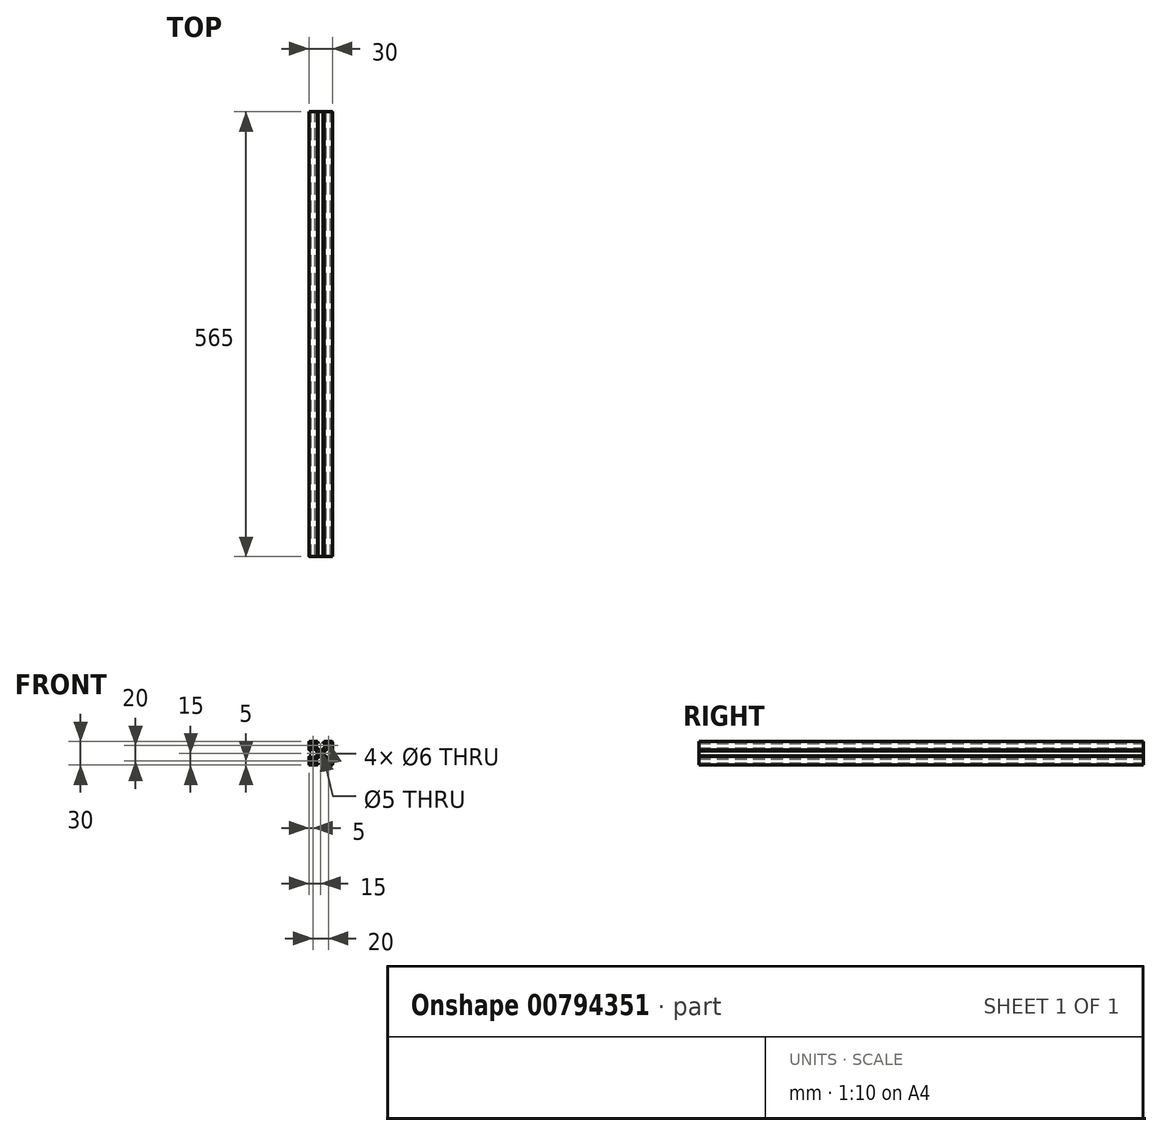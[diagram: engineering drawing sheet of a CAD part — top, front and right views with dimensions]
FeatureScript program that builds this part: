
annotation { "Feature Type Name" : "Feature", "Feature Type Description" : "" }
export const myFeature = defineFeature(function(context is Context, id is Id, definition is map)
    precondition{}
    {
        {
            var Q0;
            Q0=qCreatedBy(makeId("Front.planeOp"),FACE);
            var sketch = newSketch(context, id + "F0", { "sketchPlane" : qUnion([Q0])});
            skCircle(sketch, "E0", {"center": v(0, 0) * mm, "radius": 2.5 * mm});
            skCircle(sketch, "E1", {"center": v(-10, 10) * mm, "radius": 3 * mm});
            skCircle(sketch, "E2", {"center": v(10, 10) * mm, "radius": 3 * mm});
            skCircle(sketch, "E3", {"center": v(10, -10) * mm, "radius": 3 * mm});
            skCircle(sketch, "E4", {"center": v(-10, -10) * mm, "radius": 3 * mm});
            skLineSegment(sketch, "E5.bottom", {"start": v(-14, 15) * mm, "end": v(-4.5, 15) * mm});
            skLineSegment(sketch, "E5.top", {"start": v(-14, -15) * mm, "end": v(-4.2, -15) * mm});
            skLineSegment(sketch, "E5.left", {"start": v(-15, 14) * mm, "end": v(-15, 4.2) * mm});
            skLineSegment(sketch, "E5.right", {"start": v(15, 14) * mm, "end": v(15, 4.2) * mm});
            skPoint(sketch, "E6.visualSharp", {"position": v(-15, 15) * mm});
            skArc(sketch, "E6.filletArc", {"start": v(-14, 15) * mm, "mid": v(-14.7, 14.7) * mm, "end": v(-15, 14) * mm});
            skPoint(sketch, "E7.visualSharp", {"position": v(-15, -15) * mm});
            skArc(sketch, "E7.filletArc", {"start": v(-15, -14) * mm, "mid": v(-14.7, -14.7) * mm, "end": v(-14, -15) * mm});
            skPoint(sketch, "E8.visualSharp", {"position": v(15, -15) * mm});
            skArc(sketch, "E8.filletArc", {"start": v(14, -15) * mm, "mid": v(14.7, -14.7) * mm, "end": v(15, -14) * mm});
            skPoint(sketch, "E9.visualSharp", {"position": v(15, 15) * mm});
            skArc(sketch, "E9.filletArc", {"start": v(15, 14) * mm, "mid": v(14.7, 14.7) * mm, "end": v(14, 15) * mm});
            skLineSegment(sketch, "E10", {"start": v(-3.25, 13.7) * mm, "end": v(-3.25, 12.5) * mm});
            skLineSegment(sketch, "E11", {"start": v(-3.25, 12.5) * mm, "end": v(-5.25, 12.5) * mm});
            skLineSegment(sketch, "E12", {"start": v(-5.25, 12.5) * mm, "end": v(-5.25, 8) * mm});
            skLineSegment(sketch, "E13", {"start": v(-4.97, 7.3) * mm, "end": v(-2.54, 4.8) * mm});
            skLineSegment(sketch, "E14", {"start": v(-1.83, 4.5) * mm, "end": v(1.83, 4.5) * mm});
            skLineSegment(sketch, "E15", {"start": v(2.54, 4.8) * mm, "end": v(4.97, 7.3) * mm});
            skLineSegment(sketch, "E16", {"start": v(5.25, 8) * mm, "end": v(5.25, 12.5) * mm});
            skLineSegment(sketch, "E17", {"start": v(5.25, 12.5) * mm, "end": v(3.25, 12.5) * mm});
            skLineSegment(sketch, "E18", {"start": v(3.25, 12.5) * mm, "end": v(3.25, 13.7) * mm});
            skLineSegment(sketch, "E19.trimOffspring", {"start": v(4.5, 15) * mm, "end": v(14, 15) * mm});
            skPoint(sketch, "E20.visualSharp", {"position": v(-5.25, 7.6) * mm});
            skArc(sketch, "E20.filletArc", {"start": v(-5.25, 8) * mm, "mid": v(-5.18, 7.63) * mm, "end": v(-4.97, 7.3) * mm});
            skPoint(sketch, "E21.visualSharp", {"position": v(-2.25, 4.5) * mm});
            skArc(sketch, "E21.filletArc", {"start": v(-2.54, 4.8) * mm, "mid": v(-2.22, 4.58) * mm, "end": v(-1.83, 4.5) * mm});
            skPoint(sketch, "E22.visualSharp", {"position": v(2.25, 4.5) * mm});
            skArc(sketch, "E22.filletArc", {"start": v(1.83, 4.5) * mm, "mid": v(2.22, 4.58) * mm, "end": v(2.54, 4.8) * mm});
            skPoint(sketch, "E23.visualSharp", {"position": v(5.25, 7.6) * mm});
            skArc(sketch, "E23.filletArc", {"start": v(4.97, 7.3) * mm, "mid": v(5.18, 7.63) * mm, "end": v(5.25, 8) * mm});
            skLineSegment(sketch, "E24", {"start": v(-3.55, 14) * mm, "end": v(-3.7, 14) * mm});
            skLineSegment(sketch, "E25", {"start": v(-4.2, 14.5) * mm, "end": v(-4.2, 14.7) * mm});
            skLineSegment(sketch, "E26", {"start": v(3.55, 14) * mm, "end": v(3.7, 14) * mm});
            skLineSegment(sketch, "E27", {"start": v(4.2, 14.5) * mm, "end": v(4.2, 14.7) * mm});
            skPoint(sketch, "E28.visualSharp", {"position": v(-4.2, 15) * mm});
            skArc(sketch, "E28.filletArc", {"start": v(-4.2, 14.7) * mm, "mid": v(-4.29, 14.91) * mm, "end": v(-4.5, 15) * mm});
            skPoint(sketch, "E29.visualSharp", {"position": v(-3.25, 14) * mm});
            skArc(sketch, "E29.filletArc", {"start": v(-3.25, 13.7) * mm, "mid": v(-3.34, 13.91) * mm, "end": v(-3.55, 14) * mm});
            skPoint(sketch, "E30.visualSharp", {"position": v(3.25, 14) * mm});
            skArc(sketch, "E30.filletArc", {"start": v(3.55, 14) * mm, "mid": v(3.34, 13.91) * mm, "end": v(3.25, 13.7) * mm});
            skPoint(sketch, "E31.visualSharp", {"position": v(4.2, 15) * mm});
            skArc(sketch, "E31.filletArc", {"start": v(4.5, 15) * mm, "mid": v(4.29, 14.91) * mm, "end": v(4.2, 14.7) * mm});
            skPoint(sketch, "E32.visualSharp", {"position": v(4.2, 14) * mm});
            skArc(sketch, "E32.filletArc", {"start": v(3.7, 14) * mm, "mid": v(4.05, 14.15) * mm, "end": v(4.2, 14.5) * mm});
            skPoint(sketch, "E33.visualSharp", {"position": v(-4.2, 14) * mm});
            skArc(sketch, "E33.filletArc", {"start": v(-4.2, 14.5) * mm, "mid": v(-4.05, 14.15) * mm, "end": v(-3.7, 14) * mm});
            skPoint(sketch, "E34.1.0", {"position": v(-14, 3.25) * mm});
            skLineSegment(sketch, "E34.1.1", {"start": v(-12.5, -3.25) * mm, "end": v(-12.5, -5.25) * mm});
            skPoint(sketch, "E34.1.2", {"position": v(-15, 4.2) * mm});
            skPoint(sketch, "E34.1.3", {"position": v(-14, 4.2) * mm});
            skLineSegment(sketch, "E34.1.4", {"start": v(-12.5, -5.25) * mm, "end": v(-8, -5.25) * mm});
            skLineSegment(sketch, "E34.1.5", {"start": v(-4.8, 2.54) * mm, "end": v(-7.3, 4.97) * mm});
            skLineSegment(sketch, "E34.1.6", {"start": v(-12.5, 5.25) * mm, "end": v(-12.5, 3.25) * mm});
            skPoint(sketch, "E34.1.7", {"position": v(-15, -4.2) * mm});
            skPoint(sketch, "E34.1.8", {"position": v(-7.6, -5.25) * mm});
            skLineSegment(sketch, "E34.1.9", {"start": v(-8, 5.25) * mm, "end": v(-12.5, 5.25) * mm});
            skPoint(sketch, "E34.1.10", {"position": v(-14, -3.25) * mm});
            skPoint(sketch, "E34.1.11", {"position": v(-7.6, 5.25) * mm});
            skLineSegment(sketch, "E34.1.12", {"start": v(-4.5, -1.83) * mm, "end": v(-4.5, 1.83) * mm});
            skPoint(sketch, "E34.1.13", {"position": v(-4.5, 2.25) * mm});
            skPoint(sketch, "E34.1.14", {"position": v(-4.5, -2.25) * mm});
            skPoint(sketch, "E34.1.15", {"position": v(-14, -4.2) * mm});
            skLineSegment(sketch, "E34.1.16", {"start": v(-12.5, 3.25) * mm, "end": v(-13.7, 3.25) * mm});
            skLineSegment(sketch, "E34.1.17", {"start": v(-7.3, -4.97) * mm, "end": v(-4.8, -2.54) * mm});
            skLineSegment(sketch, "E34.1.18", {"start": v(-13.7, -3.25) * mm, "end": v(-12.5, -3.25) * mm});
            skArc(sketch, "E34.1.19", {"start": v(-14.5, -4.2) * mm, "mid": v(-14.15, -4.05) * mm, "end": v(-14, -3.7) * mm});
            skArc(sketch, "E34.1.20", {"start": v(-4.5, 1.83) * mm, "mid": v(-4.58, 2.22) * mm, "end": v(-4.8, 2.54) * mm});
            skArc(sketch, "E34.1.21", {"start": v(-8, -5.25) * mm, "mid": v(-7.63, -5.18) * mm, "end": v(-7.3, -4.97) * mm});
            skArc(sketch, "E34.1.22", {"start": v(-4.8, -2.54) * mm, "mid": v(-4.58, -2.22) * mm, "end": v(-4.5, -1.83) * mm});
            skArc(sketch, "E34.1.23", {"start": v(-7.3, 4.97) * mm, "mid": v(-7.63, 5.18) * mm, "end": v(-8, 5.25) * mm});
            skArc(sketch, "E34.1.24", {"start": v(-14, 3.55) * mm, "mid": v(-13.91, 3.34) * mm, "end": v(-13.7, 3.25) * mm});
            skLineSegment(sketch, "E34.1.25", {"start": v(-14, -3.55) * mm, "end": v(-14, -3.7) * mm});
            skArc(sketch, "E34.1.26", {"start": v(-14, 3.7) * mm, "mid": v(-14.15, 4.05) * mm, "end": v(-14.5, 4.2) * mm});
            skArc(sketch, "E34.1.27", {"start": v(-14.7, -4.2) * mm, "mid": v(-14.91, -4.29) * mm, "end": v(-15, -4.5) * mm});
            skArc(sketch, "E34.1.28", {"start": v(-13.7, -3.25) * mm, "mid": v(-13.91, -3.34) * mm, "end": v(-14, -3.55) * mm});
            skArc(sketch, "E34.1.29", {"start": v(-15, 4.5) * mm, "mid": v(-14.91, 4.29) * mm, "end": v(-14.7, 4.2) * mm});
            skLineSegment(sketch, "E34.1.30", {"start": v(-14.5, 4.2) * mm, "end": v(-14.7, 4.2) * mm});
            skLineSegment(sketch, "E34.1.31", {"start": v(-14.5, -4.2) * mm, "end": v(-14.7, -4.2) * mm});
            skLineSegment(sketch, "E34.1.32", {"start": v(-14, 3.55) * mm, "end": v(-14, 3.7) * mm});
            skPoint(sketch, "E34.2.0", {"position": v(-3.25, -14) * mm});
            skLineSegment(sketch, "E34.2.1", {"start": v(3.25, -12.5) * mm, "end": v(5.25, -12.5) * mm});
            skPoint(sketch, "E34.2.2", {"position": v(-4.2, -15) * mm});
            skPoint(sketch, "E34.2.3", {"position": v(-4.2, -14) * mm});
            skLineSegment(sketch, "E34.2.4", {"start": v(5.25, -12.5) * mm, "end": v(5.25, -8) * mm});
            skLineSegment(sketch, "E34.2.5", {"start": v(-2.54, -4.8) * mm, "end": v(-4.97, -7.3) * mm});
            skLineSegment(sketch, "E34.2.6", {"start": v(-5.25, -12.5) * mm, "end": v(-3.25, -12.5) * mm});
            skPoint(sketch, "E34.2.7", {"position": v(4.2, -15) * mm});
            skPoint(sketch, "E34.2.8", {"position": v(5.25, -7.6) * mm});
            skLineSegment(sketch, "E34.2.9", {"start": v(-5.25, -8) * mm, "end": v(-5.25, -12.5) * mm});
            skPoint(sketch, "E34.2.10", {"position": v(3.25, -14) * mm});
            skPoint(sketch, "E34.2.11", {"position": v(-5.25, -7.6) * mm});
            skLineSegment(sketch, "E34.2.12", {"start": v(1.83, -4.5) * mm, "end": v(-1.83, -4.5) * mm});
            skPoint(sketch, "E34.2.13", {"position": v(-2.25, -4.5) * mm});
            skPoint(sketch, "E34.2.14", {"position": v(2.25, -4.5) * mm});
            skPoint(sketch, "E34.2.15", {"position": v(4.2, -14) * mm});
            skLineSegment(sketch, "E34.2.16", {"start": v(-3.25, -12.5) * mm, "end": v(-3.25, -13.7) * mm});
            skLineSegment(sketch, "E34.2.17", {"start": v(4.97, -7.3) * mm, "end": v(2.54, -4.8) * mm});
            skLineSegment(sketch, "E34.2.18", {"start": v(3.25, -13.7) * mm, "end": v(3.25, -12.5) * mm});
            skArc(sketch, "E34.2.19", {"start": v(4.2, -14.5) * mm, "mid": v(4.05, -14.15) * mm, "end": v(3.7, -14) * mm});
            skArc(sketch, "E34.2.20", {"start": v(-1.83, -4.5) * mm, "mid": v(-2.22, -4.58) * mm, "end": v(-2.54, -4.8) * mm});
            skArc(sketch, "E34.2.21", {"start": v(5.25, -8) * mm, "mid": v(5.18, -7.63) * mm, "end": v(4.97, -7.3) * mm});
            skArc(sketch, "E34.2.22", {"start": v(2.54, -4.8) * mm, "mid": v(2.22, -4.58) * mm, "end": v(1.83, -4.5) * mm});
            skArc(sketch, "E34.2.23", {"start": v(-4.97, -7.3) * mm, "mid": v(-5.18, -7.63) * mm, "end": v(-5.25, -8) * mm});
            skArc(sketch, "E34.2.24", {"start": v(-3.55, -14) * mm, "mid": v(-3.34, -13.91) * mm, "end": v(-3.25, -13.7) * mm});
            skLineSegment(sketch, "E34.2.25", {"start": v(3.55, -14) * mm, "end": v(3.7, -14) * mm});
            skArc(sketch, "E34.2.26", {"start": v(-3.7, -14) * mm, "mid": v(-4.05, -14.15) * mm, "end": v(-4.2, -14.5) * mm});
            skArc(sketch, "E34.2.27", {"start": v(4.2, -14.7) * mm, "mid": v(4.29, -14.91) * mm, "end": v(4.5, -15) * mm});
            skArc(sketch, "E34.2.28", {"start": v(3.25, -13.7) * mm, "mid": v(3.34, -13.91) * mm, "end": v(3.55, -14) * mm});
            skArc(sketch, "E34.2.29", {"start": v(-4.5, -15) * mm, "mid": v(-4.29, -14.91) * mm, "end": v(-4.2, -14.7) * mm});
            skLineSegment(sketch, "E34.2.30", {"start": v(-4.2, -14.5) * mm, "end": v(-4.2, -14.7) * mm});
            skLineSegment(sketch, "E34.2.31", {"start": v(4.2, -14.5) * mm, "end": v(4.2, -14.7) * mm});
            skLineSegment(sketch, "E34.2.32", {"start": v(-3.55, -14) * mm, "end": v(-3.7, -14) * mm});
            skPoint(sketch, "E34.3.0", {"position": v(14, -3.25) * mm});
            skLineSegment(sketch, "E34.3.1", {"start": v(12.5, 3.25) * mm, "end": v(12.5, 5.25) * mm});
            skPoint(sketch, "E34.3.2", {"position": v(15, -4.2) * mm});
            skPoint(sketch, "E34.3.3", {"position": v(14, -4.2) * mm});
            skLineSegment(sketch, "E34.3.4", {"start": v(12.5, 5.25) * mm, "end": v(8, 5.25) * mm});
            skLineSegment(sketch, "E34.3.5", {"start": v(4.8, -2.54) * mm, "end": v(7.3, -4.97) * mm});
            skLineSegment(sketch, "E34.3.6", {"start": v(12.5, -5.25) * mm, "end": v(12.5, -3.25) * mm});
            skPoint(sketch, "E34.3.7", {"position": v(15, 4.2) * mm});
            skPoint(sketch, "E34.3.8", {"position": v(7.6, 5.25) * mm});
            skLineSegment(sketch, "E34.3.9", {"start": v(8, -5.25) * mm, "end": v(12.5, -5.25) * mm});
            skPoint(sketch, "E34.3.10", {"position": v(14, 3.25) * mm});
            skPoint(sketch, "E34.3.11", {"position": v(7.6, -5.25) * mm});
            skLineSegment(sketch, "E34.3.12", {"start": v(4.5, 1.83) * mm, "end": v(4.5, -1.83) * mm});
            skPoint(sketch, "E34.3.13", {"position": v(4.5, -2.25) * mm});
            skPoint(sketch, "E34.3.14", {"position": v(4.5, 2.25) * mm});
            skPoint(sketch, "E34.3.15", {"position": v(14, 4.2) * mm});
            skLineSegment(sketch, "E34.3.16", {"start": v(12.5, -3.25) * mm, "end": v(13.7, -3.25) * mm});
            skLineSegment(sketch, "E34.3.17", {"start": v(7.3, 4.97) * mm, "end": v(4.8, 2.54) * mm});
            skLineSegment(sketch, "E34.3.18", {"start": v(13.7, 3.25) * mm, "end": v(12.5, 3.25) * mm});
            skArc(sketch, "E34.3.19", {"start": v(14.5, 4.2) * mm, "mid": v(14.15, 4.05) * mm, "end": v(14, 3.7) * mm});
            skArc(sketch, "E34.3.20", {"start": v(4.5, -1.83) * mm, "mid": v(4.58, -2.22) * mm, "end": v(4.8, -2.54) * mm});
            skArc(sketch, "E34.3.21", {"start": v(8, 5.25) * mm, "mid": v(7.63, 5.18) * mm, "end": v(7.3, 4.97) * mm});
            skArc(sketch, "E34.3.22", {"start": v(4.8, 2.54) * mm, "mid": v(4.58, 2.22) * mm, "end": v(4.5, 1.83) * mm});
            skArc(sketch, "E34.3.23", {"start": v(7.3, -4.97) * mm, "mid": v(7.63, -5.18) * mm, "end": v(8, -5.25) * mm});
            skArc(sketch, "E34.3.24", {"start": v(14, -3.55) * mm, "mid": v(13.91, -3.34) * mm, "end": v(13.7, -3.25) * mm});
            skLineSegment(sketch, "E34.3.25", {"start": v(14, 3.55) * mm, "end": v(14, 3.7) * mm});
            skArc(sketch, "E34.3.26", {"start": v(14, -3.7) * mm, "mid": v(14.15, -4.05) * mm, "end": v(14.5, -4.2) * mm});
            skArc(sketch, "E34.3.27", {"start": v(14.7, 4.2) * mm, "mid": v(14.91, 4.29) * mm, "end": v(15, 4.5) * mm});
            skArc(sketch, "E34.3.28", {"start": v(13.7, 3.25) * mm, "mid": v(13.91, 3.34) * mm, "end": v(14, 3.55) * mm});
            skArc(sketch, "E34.3.29", {"start": v(15, -4.5) * mm, "mid": v(14.91, -4.29) * mm, "end": v(14.7, -4.2) * mm});
            skLineSegment(sketch, "E34.3.30", {"start": v(14.5, -4.2) * mm, "end": v(14.7, -4.2) * mm});
            skLineSegment(sketch, "E34.3.31", {"start": v(14.5, 4.2) * mm, "end": v(14.7, 4.2) * mm});
            skLineSegment(sketch, "E34.3.32", {"start": v(14, -3.55) * mm, "end": v(14, -3.7) * mm});
            skLineSegment(sketch, "E35.trimOffspring", {"start": v(-15, -4.2) * mm, "end": v(-15, -14) * mm});
            skLineSegment(sketch, "E36.trimOffspring", {"start": v(15, -4.2) * mm, "end": v(15, -14) * mm});
            skLineSegment(sketch, "E37.trimOffspring", {"start": v(4.2, -15) * mm, "end": v(14, -15) * mm});
            skSolve(sketch);
        }
        {
            var Q0;
            Q0=makeQuery(id+"F0.imprint","IMPRINT",FACE,{"disambiguationData":[TD([[makeQuery(id+"F0.imprint","IMPRINT",EDGE,{"derivedFrom":sQuery(id+"F0.wireOp",EDGE,"E0")}),-1.0]])]});
            extrude(context, id + "F1", {"entities" : qUnion([Q0]), "depth" : 565 * mm, "offsetDistance" : 25 * mm});
        }
    });
